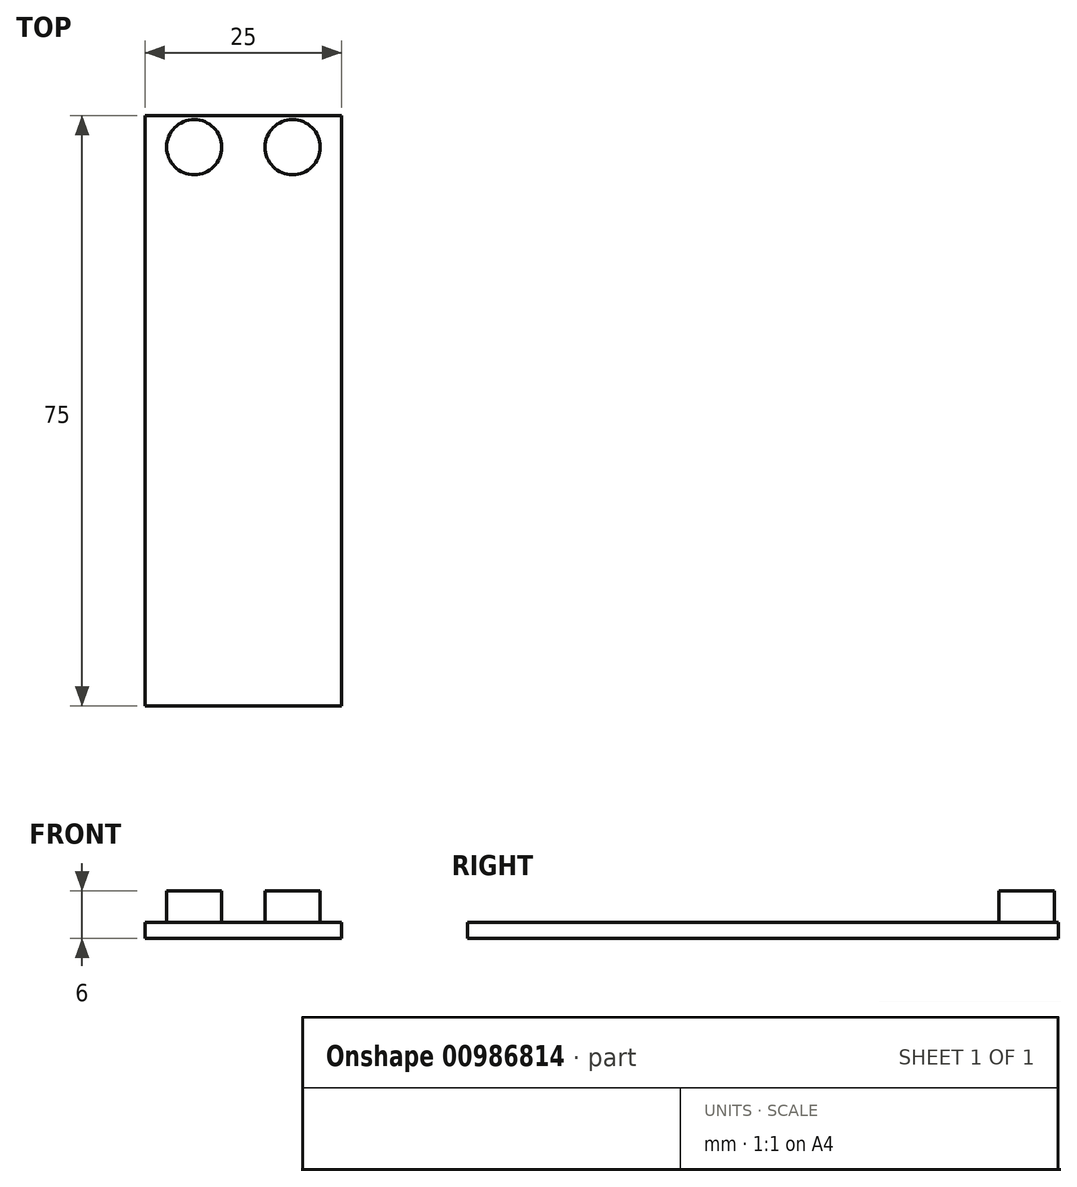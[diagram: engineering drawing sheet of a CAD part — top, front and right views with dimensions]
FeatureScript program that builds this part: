
annotation { "Feature Type Name" : "Feature", "Feature Type Description" : "" }
export const myFeature = defineFeature(function(context is Context, id is Id, definition is map)
    precondition{}
    {
        {
            var Q0;
            Q0=qCreatedBy(makeId("Top.planeOp"),FACE);
            var sketch = newSketch(context, id + "F0", { "sketchPlane" : qUnion([Q0])});
            skLineSegment(sketch, "E0.bottom", {"start": v(0, 0) * mm, "end": v(25, 0) * mm});
            skLineSegment(sketch, "E0.top", {"start": v(0, 75) * mm, "end": v(25, 75) * mm});
            skLineSegment(sketch, "E0.left", {"start": v(0, 0) * mm, "end": v(0, 75) * mm});
            skLineSegment(sketch, "E0.right", {"start": v(25, 0) * mm, "end": v(25, 75) * mm});
            skSolve(sketch);
        }
        {
            var Q0;
            Q0=makeQuery(id+"F0.imprint","IMPRINT",FACE,{"disambiguationData":[TD([[makeQuery(id+"F0.imprint","IMPRINT",EDGE,{"derivedFrom":sQuery(id+"F0.wireOp",EDGE,"E0.bottom")}),1.0]])]});
            extrude(context, id + "F1", {"entities" : qUnion([Q0]), "depth" : 2 * mm, "offsetDistance" : 25 * mm});
        }
        {
            var Q0;
            Q0=makeQuery(id+"F1.opExtrude","CAP_FACE",FACE,{"disambiguationData":[OSD([sQuery(id+"F0.wireOp",EDGE,"E0.bottom"),sQuery(id+"F0.wireOp",EDGE,"E0.top"),sQuery(id+"F0.wireOp",EDGE,"E0.left"),sQuery(id+"F0.wireOp",EDGE,"E0.right")])],"isStart":false});
            var sketch = newSketch(context, id + "F2", { "sketchPlane" : qUnion([Q0])});
            skPoint(sketch, "E1", {"position": v(12.5, 75) * mm});
            skPoint(sketch, "E2", {"position": v(0, 37.5) * mm});
            skPoint(sketch, "E3", {"position": v(25, 37.5) * mm});
            skPoint(sketch, "E4", {"position": v(12.5, 0) * mm});
            skPoint(sketch, "E5", {"position": v(6.25, 75) * mm});
            skPoint(sketch, "E6", {"position": v(18.75, 75) * mm});
            skPoint(sketch, "E7", {"position": v(12.5, 71) * mm});
            skPoint(sketch, "E8", {"position": v(6.25, 71) * mm});
            skPoint(sketch, "E9", {"position": v(18.75, 71) * mm});
            skCircle(sketch, "E10", {"center": v(6.25, 71) * mm, "radius": 3.5 * mm});
            skCircle(sketch, "E11", {"center": v(18.75, 71) * mm, "radius": 3.5 * mm});
            skSolve(sketch);
        }
        {
            var Q0;
            Q0=makeQuery(id+"F2.imprint","IMPRINT",FACE,{"disambiguationData":[TD([[makeQuery(id+"F2.imprint","IMPRINT",EDGE,{"derivedFrom":sQuery(id+"F2.wireOp",EDGE,"E10")}),1.0]])]});
            var Q1;
            Q1=makeQuery(id+"F2.imprint","IMPRINT",FACE,{"disambiguationData":[TD([[makeQuery(id+"F2.imprint","IMPRINT",EDGE,{"derivedFrom":sQuery(id+"F2.wireOp",EDGE,"E11")}),1.0]])]});
            extrude(context, id + "F3", {"entities" : qUnion([Q0, Q1]), "operationType" : NewBodyOperationType.ADD, "depth" : 4 * mm, "offsetDistance" : 25 * mm});
        }
    });
